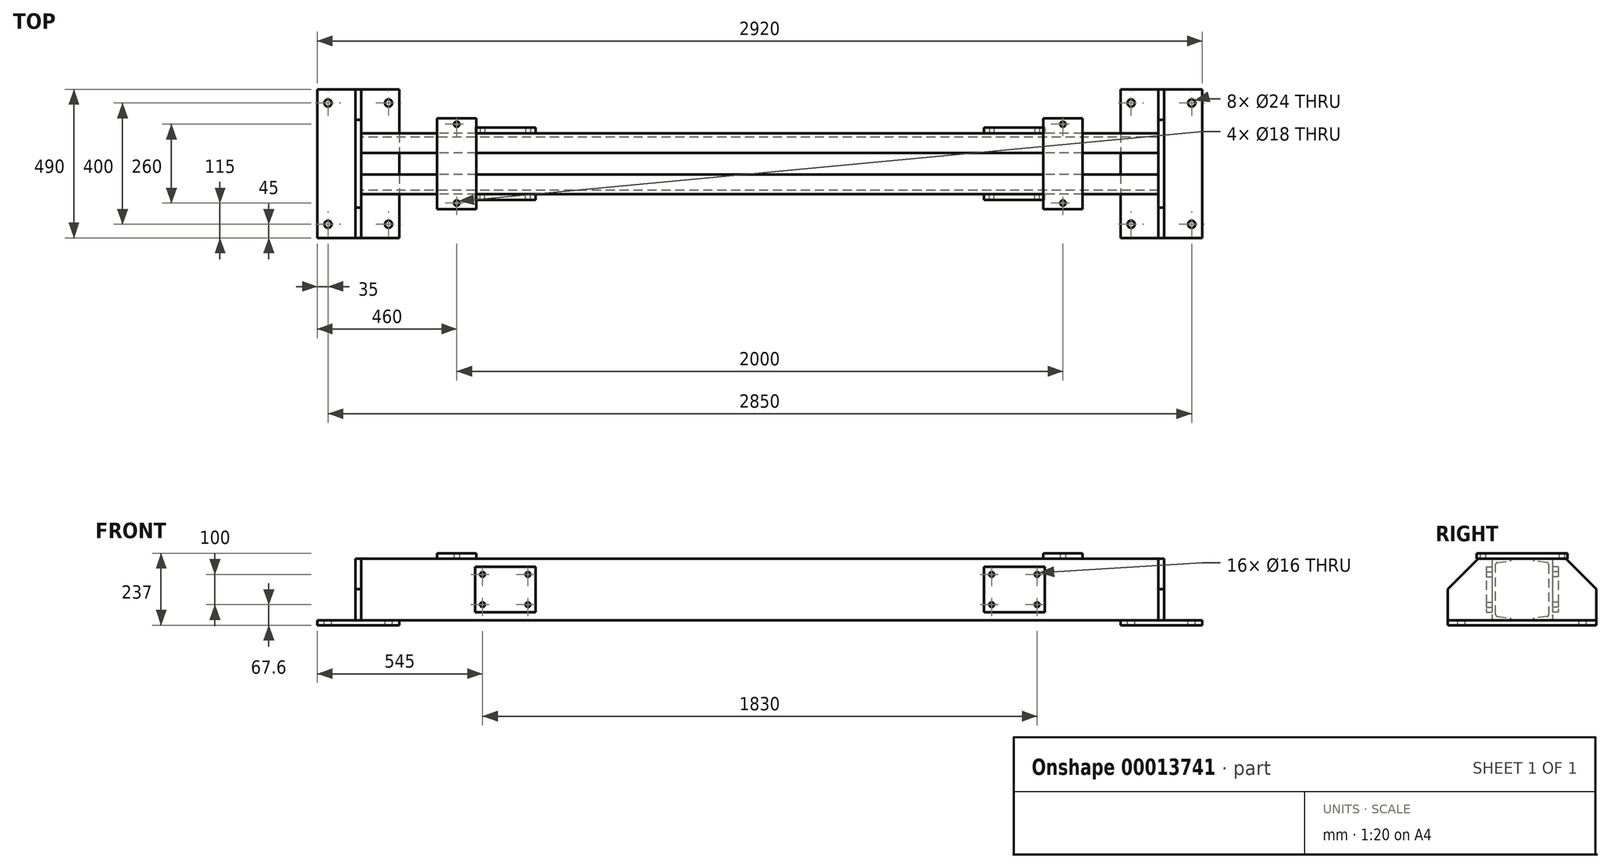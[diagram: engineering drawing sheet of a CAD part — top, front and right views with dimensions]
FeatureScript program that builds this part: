
annotation { "Feature Type Name" : "Feature", "Feature Type Description" : "" }
export const myFeature = defineFeature(function(context is Context, id is Id, definition is map)
    precondition{}
    {
        {
            var Q0;
            Q0=qCreatedBy(makeId("Right.planeOp"),FACE);
            var sketch = newSketch(context, id + "F0", { "sketchPlane" : qUnion([Q0])});
            skLineSegment(sketch, "E0", {"start": v(0, 81.85) * mm, "end": v(0, -95.58) * mm, "construction": true});
            skLineSegment(sketch, "E1", {"start": v(-119.35, 0) * mm, "end": v(122.16, 0) * mm, "construction": true});
            skLineSegment(sketch, "E2.0", {"start": v(-100, 101.6) * mm, "end": v(-100, 0) * mm});
            skLineSegment(sketch, "E3.0", {"start": v(-100, 101.6) * mm, "end": v(-35.8, 101.6) * mm});
            skLineSegment(sketch, "E4.0", {"start": v(-87.6, 82.16) * mm, "end": v(-87.6, 0) * mm});
            skLineSegment(sketch, "E5.0", {"start": v(-35.8, 88.1) * mm, "end": v(122.16, 88.1) * mm, "construction": true});
            skLineSegment(sketch, "E6.0", {"start": v(-35.8, 101.6) * mm, "end": v(-35.8, 99.47) * mm});
            skLineSegment(sketch, "E7", {"start": v(-81.71, 88.9) * mm, "end": v(-40.13, 94.51) * mm});
            skPoint(sketch, "E8.visualSharp", {"position": v(-35.8, 95.1) * mm});
            skArc(sketch, "E8.filletArc", {"start": v(-40.13, 94.51) * mm, "mid": v(-37.04, 96.18) * mm, "end": v(-35.8, 99.47) * mm});
            skPoint(sketch, "E9.visualSharp", {"position": v(-87.6, 88.1) * mm});
            skArc(sketch, "E9.filletArc", {"start": v(-81.71, 88.9) * mm, "mid": v(-85.92, 86.63) * mm, "end": v(-87.6, 82.16) * mm});
            skArc(sketch, "E10.0.MirrorCS", {"start": v(-40.13, -94.51) * mm, "mid": v(-37.04, -96.18) * mm, "end": v(-35.8, -99.47) * mm});
            skLineSegment(sketch, "E10.1.MirrorCS", {"start": v(-35.8, -101.6) * mm, "end": v(-35.8, -99.47) * mm});
            skArc(sketch, "E10.2.MirrorCS", {"start": v(-81.71, -88.9) * mm, "mid": v(-85.92, -86.63) * mm, "end": v(-87.6, -82.16) * mm});
            skPoint(sketch, "E10.3.MirrorP", {"position": v(-87.6, -88.1) * mm});
            skLineSegment(sketch, "E10.4.MirrorCS", {"start": v(-100, -101.6) * mm, "end": v(-100, 0) * mm});
            skLineSegment(sketch, "E10.5.MirrorCS", {"start": v(-87.6, -82.16) * mm, "end": v(-87.6, 0) * mm});
            skLineSegment(sketch, "E10.6.MirrorCS", {"start": v(-81.71, -88.9) * mm, "end": v(-40.13, -94.51) * mm});
            skLineSegment(sketch, "E10.7.MirrorCS", {"start": v(-100, -101.6) * mm, "end": v(-35.8, -101.6) * mm});
            skPoint(sketch, "E10.8.MirrorP", {"position": v(-35.8, -95.1) * mm});
            skLineSegment(sketch, "E11.0.MirrorCS", {"start": v(35.8, -101.6) * mm, "end": v(35.8, -99.47) * mm});
            skArc(sketch, "E11.1.MirrorCS", {"start": v(40.13, 94.51) * mm, "mid": v(37.04, 96.18) * mm, "end": v(35.8, 99.47) * mm});
            skLineSegment(sketch, "E11.2.MirrorCS", {"start": v(35.8, 101.6) * mm, "end": v(35.8, 99.47) * mm});
            skArc(sketch, "E11.3.MirrorCS", {"start": v(40.13, -94.51) * mm, "mid": v(37.04, -96.18) * mm, "end": v(35.8, -99.47) * mm});
            skArc(sketch, "E11.4.MirrorCS", {"start": v(81.71, 88.9) * mm, "mid": v(85.92, 86.63) * mm, "end": v(87.6, 82.16) * mm});
            skArc(sketch, "E11.5.MirrorCS", {"start": v(81.71, -88.9) * mm, "mid": v(85.92, -86.63) * mm, "end": v(87.6, -82.16) * mm});
            skLineSegment(sketch, "E11.6.MirrorCS", {"start": v(100, -101.6) * mm, "end": v(35.8, -101.6) * mm});
            skLineSegment(sketch, "E11.7.MirrorCS", {"start": v(100, -101.6) * mm, "end": v(100, 0) * mm});
            skLineSegment(sketch, "E11.8.MirrorCS", {"start": v(81.71, -88.9) * mm, "end": v(40.13, -94.51) * mm});
            skLineSegment(sketch, "E11.9.MirrorCS", {"start": v(87.6, -82.16) * mm, "end": v(87.6, 0) * mm});
            skPoint(sketch, "E11.10.MirrorP", {"position": v(87.6, -88.1) * mm});
            skPoint(sketch, "E11.11.MirrorP", {"position": v(35.8, 95.1) * mm});
            skPoint(sketch, "E11.12.MirrorP", {"position": v(35.8, -95.1) * mm});
            skLineSegment(sketch, "E11.13.MirrorCS", {"start": v(81.71, 88.9) * mm, "end": v(40.13, 94.51) * mm});
            skLineSegment(sketch, "E11.14.MirrorCS", {"start": v(100, 101.6) * mm, "end": v(35.8, 101.6) * mm});
            skPoint(sketch, "E11.15.MirrorP", {"position": v(87.6, 88.1) * mm});
            skLineSegment(sketch, "E11.16.MirrorCS", {"start": v(100, 101.6) * mm, "end": v(100, 0) * mm});
            skLineSegment(sketch, "E11.17.MirrorCS", {"start": v(87.6, 82.16) * mm, "end": v(87.6, 0) * mm});
            skSolve(sketch);
        }
        {
            var Q0;
            Q0=qSketchRegion(id+"F0",true);
            extrude(context, id + "F1", {"entities" : qUnion([Q0]), "endBound" : BoundingType.SYMMETRIC, "depth" : 2631 * mm});
        }
        {
            var Q0;
            Q0=makeQuery(id+"F1.opExtrude","CAP_FACE",FACE,{"disambiguationData":[OSD([sQuery(id+"F0.wireOp",EDGE,"E2.0"),sQuery(id+"F0.wireOp",EDGE,"E3.0"),sQuery(id+"F0.wireOp",EDGE,"E4.0"),sQuery(id+"F0.wireOp",EDGE,"E6.0"),sQuery(id+"F0.wireOp",EDGE,"E7"),sQuery(id+"F0.wireOp",EDGE,"E8.filletArc"),sQuery(id+"F0.wireOp",EDGE,"E9.filletArc"),sQuery(id+"F0.wireOp",EDGE,"E10.0.MirrorCS"),sQuery(id+"F0.wireOp",EDGE,"E10.1.MirrorCS"),sQuery(id+"F0.wireOp",EDGE,"E10.2.MirrorCS"),sQuery(id+"F0.wireOp",EDGE,"E10.4.MirrorCS"),sQuery(id+"F0.wireOp",EDGE,"E10.5.MirrorCS"),sQuery(id+"F0.wireOp",EDGE,"E10.6.MirrorCS"),sQuery(id+"F0.wireOp",EDGE,"E10.7.MirrorCS")])],"isStart":false});
            var sketch = newSketch(context, id + "F2", { "sketchPlane" : qUnion([Q0])});
            skLineSegment(sketch, "E12", {"start": v(0, 0) * mm, "end": v(0, -156.9) * mm, "construction": true});
            skLineSegment(sketch, "E13.0", {"start": v(-245, 1.6) * mm, "end": v(-245, -101.6) * mm});
            skLineSegment(sketch, "E14.0", {"start": v(-245, -101.6) * mm, "end": v(0, -101.6) * mm});
            skLineSegment(sketch, "E15.0", {"start": v(-145, 101.6) * mm, "end": v(0, 101.6) * mm});
            skPoint(sketch, "E16.orphan", {"position": v(-100, -101.6) * mm});
            skPoint(sketch, "E17.orphan", {"position": v(-100, 101.6) * mm});
            skPoint(sketch, "E18.orphan", {"position": v(-35.8, 101.6) * mm});
            skPoint(sketch, "E19.orphan", {"position": v(-35.8, -101.6) * mm});
            skLineSegment(sketch, "E20.0", {"start": v(-145, 101.6) * mm, "end": v(-145, -101.6) * mm, "construction": true});
            skLineSegment(sketch, "E21.0", {"start": v(-245, 1.6) * mm, "end": v(0, 1.6) * mm, "construction": true});
            skLineSegment(sketch, "E22", {"start": v(-245, 1.6) * mm, "end": v(-145, 101.6) * mm});
            skLineSegment(sketch, "E23.0.MirrorCS", {"start": v(245, 1.6) * mm, "end": v(245, -101.6) * mm});
            skLineSegment(sketch, "E23.1.MirrorCS", {"start": v(245, -101.6) * mm, "end": v(0, -101.6) * mm});
            skLineSegment(sketch, "E24.0.MirrorCS", {"start": v(245, 1.6) * mm, "end": v(145, 101.6) * mm});
            skLineSegment(sketch, "E25.0.MirrorCS", {"start": v(145, 101.6) * mm, "end": v(0, 101.6) * mm});
            skSolve(sketch);
        }
        {
            var Q0;
            Q0=qSketchRegion(id+"F2",true);
            extrude(context, id + "F3", {"entities" : qUnion([Q0]), "depth" : 19 * mm});
        }
        {
            var Q0;
            Q0=makeQuery(id+"F3.opExtrude","SWEPT_BODY",BODY,{"disambiguationData":[OSD([sQuery(id+"F2.wireOp",EDGE,"E13.0"),sQuery(id+"F2.wireOp",EDGE,"E14.0"),sQuery(id+"F2.wireOp",EDGE,"E15.0"),sQuery(id+"F2.wireOp",EDGE,"E22"),sQuery(id+"F2.wireOp",EDGE,"E23.0.MirrorCS"),sQuery(id+"F2.wireOp",EDGE,"E23.1.MirrorCS"),sQuery(id+"F2.wireOp",EDGE,"E24.0.MirrorCS"),sQuery(id+"F2.wireOp",EDGE,"E25.0.MirrorCS")])]});
            var Q1;
            Q1=qCreatedBy(makeId("Right.planeOp"),FACE);
            mirror(context, id + "F4", {"entities" : qUnion([Q0]), "mirrorPlane" : qUnion([Q1])});
        }
        {
            var Q0;
            Q0=makeQuery(id+"F1.opExtrude","SWEPT_FACE",FACE,{"disambiguationData":[OSD([sQuery(id+"F0.wireOp",EDGE,"E10.7.MirrorCS")])]});
            var sketch = newSketch(context, id + "F5", { "sketchPlane" : qUnion([Q0])});
            skLineSegment(sketch, "E26", {"start": v(0, 0) * mm, "end": v(0, 513.83) * mm, "construction": true});
            skLineSegment(sketch, "E27", {"start": v(0, 0) * mm, "end": v(1410.8, 0) * mm, "construction": true});
            skLineSegment(sketch, "E28.0", {"start": v(1325, 0) * mm, "end": v(1325, 513.83) * mm, "construction": true});
            skLineSegment(sketch, "E29.0", {"start": v(1460, -245) * mm, "end": v(1460, 245) * mm});
            skLineSegment(sketch, "E30.0", {"start": v(1190, 245) * mm, "end": v(1460, 245) * mm});
            skLineSegment(sketch, "E31.0.MirrorCS", {"start": v(1190, -245) * mm, "end": v(1190, 245) * mm});
            skPoint(sketch, "E32.orphan", {"position": v(1190, 513.83) * mm});
            skPoint(sketch, "E33.orphan", {"position": v(1460, 513.83) * mm});
            skLineSegment(sketch, "E34.0.MirrorCS", {"start": v(1190, -245) * mm, "end": v(1460, -245) * mm});
            skPoint(sketch, "E35.orphan", {"position": v(1460, 0) * mm});
            skPoint(sketch, "E36.orphan", {"position": v(1190, 0) * mm});
            skLineSegment(sketch, "E37.0", {"start": v(0, 200) * mm, "end": v(1425, 200) * mm, "construction": true});
            skLineSegment(sketch, "E38.0", {"start": v(1425, 0) * mm, "end": v(1425, 200) * mm, "construction": true});
            skCircle(sketch, "E39", {"center": v(1425, 200) * mm, "radius": 12 * mm});
            skCircle(sketch, "E40.0.MirrorC", {"center": v(1425, -200) * mm, "radius": 12 * mm});
            skCircle(sketch, "E41.0.MirrorC", {"center": v(1225, -200) * mm, "radius": 12 * mm});
            skCircle(sketch, "E42.0.MirrorC", {"center": v(1225, 200) * mm, "radius": 12 * mm});
            skSolve(sketch);
        }
        {
            var Q0;
            Q0=qSketchRegion(id+"F5",true);
            extrude(context, id + "F6", {"entities" : qUnion([Q0]), "depth" : 16 * mm});
        }
        {
            var Q0;
            Q0=makeQuery(id+"F6.opExtrude","SWEPT_BODY",BODY,{"disambiguationData":[OSD([sQuery(id+"F5.wireOp",EDGE,"E29.0"),sQuery(id+"F5.wireOp",EDGE,"E30.0"),sQuery(id+"F5.wireOp",EDGE,"E31.0.MirrorCS"),sQuery(id+"F5.wireOp",EDGE,"E34.0.MirrorCS"),sQuery(id+"F5.wireOp",EDGE,"E39"),sQuery(id+"F5.wireOp",EDGE,"E40.0.MirrorC"),sQuery(id+"F5.wireOp",EDGE,"E41.0.MirrorC"),sQuery(id+"F5.wireOp",EDGE,"E42.0.MirrorC")])]});
            var Q1;
            Q1=qCreatedBy(makeId("Right.planeOp"),FACE);
            mirror(context, id + "F7", {"entities" : qUnion([Q0]), "mirrorPlane" : qUnion([Q1])});
        }
        {
            var Q0;
            Q0=makeQuery(id+"F1.opExtrude","SWEPT_FACE",FACE,{"disambiguationData":[OSD([sQuery(id+"F0.wireOp",EDGE,"E11.14.MirrorCS")])]});
            var sketch = newSketch(context, id + "F8", { "sketchPlane" : qUnion([Q0])});
            skLineSegment(sketch, "E43", {"start": v(0, 0) * mm, "end": v(0, 449.39) * mm, "construction": true});
            skLineSegment(sketch, "E44", {"start": v(0, 0) * mm, "end": v(1523.6, 0) * mm, "construction": true});
            skLineSegment(sketch, "E45.0", {"start": v(1000, 0) * mm, "end": v(1000, 449.39) * mm, "construction": true});
            skLineSegment(sketch, "E46.0", {"start": v(1000, 150) * mm, "end": v(1065, 150) * mm});
            skLineSegment(sketch, "E47.0", {"start": v(1065, 0) * mm, "end": v(1065, 150) * mm});
            skLineSegment(sketch, "E48.0.MirrorCS", {"start": v(1065, 0) * mm, "end": v(1065, -150) * mm});
            skLineSegment(sketch, "E49.0.MirrorCS", {"start": v(1000, -150) * mm, "end": v(1065, -150) * mm});
            skLineSegment(sketch, "E50.0.MirrorCS", {"start": v(1000, 150) * mm, "end": v(935, 150) * mm});
            skLineSegment(sketch, "E51.0.MirrorCS", {"start": v(935, 0) * mm, "end": v(935, 150) * mm});
            skLineSegment(sketch, "E52.0.MirrorCS", {"start": v(935, 0) * mm, "end": v(935, -150) * mm});
            skLineSegment(sketch, "E53.0.MirrorCS", {"start": v(1000, -150) * mm, "end": v(935, -150) * mm});
            skLineSegment(sketch, "E54.0", {"start": v(0, 130) * mm, "end": v(1523.6, 130) * mm, "construction": true});
            skCircle(sketch, "E55", {"center": v(1000, 130) * mm, "radius": 9 * mm});
            skCircle(sketch, "E56.0.MirrorC", {"center": v(1000, -130) * mm, "radius": 9 * mm});
            skSolve(sketch);
        }
        {
            var Q0;
            Q0=qSketchRegion(id+"F8",true);
            extrude(context, id + "F9", {"entities" : qUnion([Q0]), "depth" : 17.8 * mm});
        }
        {
            var Q0;
            Q0=makeQuery(id+"F9.opExtrude","SWEPT_BODY",BODY,{"disambiguationData":[OSD([sQuery(id+"F8.wireOp",EDGE,"E46.0"),sQuery(id+"F8.wireOp",EDGE,"E47.0"),sQuery(id+"F8.wireOp",EDGE,"E48.0.MirrorCS"),sQuery(id+"F8.wireOp",EDGE,"E49.0.MirrorCS"),sQuery(id+"F8.wireOp",EDGE,"E50.0.MirrorCS"),sQuery(id+"F8.wireOp",EDGE,"E51.0.MirrorCS"),sQuery(id+"F8.wireOp",EDGE,"E52.0.MirrorCS"),sQuery(id+"F8.wireOp",EDGE,"E53.0.MirrorCS"),sQuery(id+"F8.wireOp",EDGE,"E55"),sQuery(id+"F8.wireOp",EDGE,"E56.0.MirrorC")])]});
            var Q1;
            Q1=qCreatedBy(makeId("Right.planeOp"),FACE);
            mirror(context, id + "F10", {"entities" : qUnion([Q0]), "mirrorPlane" : qUnion([Q1])});
        }
        {
            var Q0;
            Q0=makeQuery(id+"F1.opExtrude","SWEPT_FACE",FACE,{"disambiguationData":[OSD([sQuery(id+"F0.wireOp",EDGE,"E11.7.MirrorCS"),sQuery(id+"F0.wireOp",EDGE,"E11.16.MirrorCS")])]});
            var sketch = newSketch(context, id + "F11", { "sketchPlane" : qUnion([Q0])});
            skLineSegment(sketch, "E57", {"start": v(0, 268.1) * mm, "end": v(0, -305.9) * mm, "construction": true});
            skLineSegment(sketch, "E58", {"start": v(0, 0) * mm, "end": v(-1422.02, 0) * mm, "construction": true});
            skLineSegment(sketch, "E59.0", {"start": v(-840, 268.1) * mm, "end": v(-840, -305.9) * mm, "construction": true});
            skLineSegment(sketch, "E60.0", {"start": v(-840, 75) * mm, "end": v(-940, 75) * mm});
            skLineSegment(sketch, "E61.0", {"start": v(-940, 75) * mm, "end": v(-940, 0) * mm});
            skLineSegment(sketch, "E62.0.MirrorCS", {"start": v(-840, 75) * mm, "end": v(-740, 75) * mm});
            skLineSegment(sketch, "E63.0.MirrorCS", {"start": v(-740, 75) * mm, "end": v(-740, 0) * mm});
            skLineSegment(sketch, "E64.0.MirrorCS", {"start": v(-940, -75) * mm, "end": v(-940, 0) * mm});
            skLineSegment(sketch, "E65.0.MirrorCS", {"start": v(-840, -75) * mm, "end": v(-940, -75) * mm});
            skLineSegment(sketch, "E66.0.MirrorCS", {"start": v(-840, -75) * mm, "end": v(-740, -75) * mm});
            skLineSegment(sketch, "E67.0.MirrorCS", {"start": v(-740, -75) * mm, "end": v(-740, 0) * mm});
            skLineSegment(sketch, "E68.0", {"start": v(-915, 268.1) * mm, "end": v(-915, -305.9) * mm, "construction": true});
            skLineSegment(sketch, "E69.0", {"start": v(0, 50) * mm, "end": v(-1422.02, 50) * mm, "construction": true});
            skCircle(sketch, "E70", {"center": v(-915, 50) * mm, "radius": 8 * mm});
            skCircle(sketch, "E71.0.MirrorC", {"center": v(-765, 50) * mm, "radius": 8 * mm});
            skCircle(sketch, "E72.0.MirrorC", {"center": v(-915, -50) * mm, "radius": 8 * mm});
            skCircle(sketch, "E73.0.MirrorC", {"center": v(-765, -50) * mm, "radius": 8 * mm});
            skCircle(sketch, "E74.0.MirrorC", {"center": v(915, 50) * mm, "radius": 8 * mm});
            skLineSegment(sketch, "E74.1.MirrorCS", {"start": v(840, 75) * mm, "end": v(940, 75) * mm});
            skCircle(sketch, "E74.2.MirrorC", {"center": v(765, 50) * mm, "radius": 8 * mm});
            skCircle(sketch, "E74.3.MirrorC", {"center": v(915, -50) * mm, "radius": 8 * mm});
            skCircle(sketch, "E74.4.MirrorC", {"center": v(765, -50) * mm, "radius": 8 * mm});
            skLineSegment(sketch, "E74.5.MirrorCS", {"start": v(740, -75) * mm, "end": v(740, 0) * mm});
            skLineSegment(sketch, "E74.6.MirrorCS", {"start": v(840, 268.1) * mm, "end": v(840, -305.9) * mm, "construction": true});
            skLineSegment(sketch, "E74.7.MirrorCS", {"start": v(840, -75) * mm, "end": v(740, -75) * mm});
            skLineSegment(sketch, "E74.8.MirrorCS", {"start": v(0, 0) * mm, "end": v(1422.02, 0) * mm, "construction": true});
            skLineSegment(sketch, "E74.9.MirrorCS", {"start": v(740, 75) * mm, "end": v(740, 0) * mm});
            skLineSegment(sketch, "E74.10.MirrorCS", {"start": v(940, 75) * mm, "end": v(940, 0) * mm});
            skLineSegment(sketch, "E74.11.MirrorCS", {"start": v(840, 75) * mm, "end": v(740, 75) * mm});
            skLineSegment(sketch, "E74.12.MirrorCS", {"start": v(940, -75) * mm, "end": v(940, 0) * mm});
            skLineSegment(sketch, "E74.13.MirrorCS", {"start": v(0, 50) * mm, "end": v(1422.02, 50) * mm, "construction": true});
            skLineSegment(sketch, "E74.14.MirrorCS", {"start": v(915, 268.1) * mm, "end": v(915, -305.9) * mm, "construction": true});
            skLineSegment(sketch, "E74.15.MirrorCS", {"start": v(840, -75) * mm, "end": v(940, -75) * mm});
            skSolve(sketch);
        }
        {
            var Q0;
            Q0=qSketchRegion(id+"F11",true);
            extrude(context, id + "F12", {"entities" : qUnion([Q0]), "depth" : 19 * mm});
        }
        {
            var Q0;
            Q0=makeQuery(id+"F12.opExtrude","SWEPT_BODY",BODY,{"disambiguationData":[OSD([sQuery(id+"F11.wireOp",EDGE,"E60.0"),sQuery(id+"F11.wireOp",EDGE,"E61.0"),sQuery(id+"F11.wireOp",EDGE,"E62.0.MirrorCS"),sQuery(id+"F11.wireOp",EDGE,"E63.0.MirrorCS"),sQuery(id+"F11.wireOp",EDGE,"E64.0.MirrorCS"),sQuery(id+"F11.wireOp",EDGE,"E65.0.MirrorCS"),sQuery(id+"F11.wireOp",EDGE,"E66.0.MirrorCS"),sQuery(id+"F11.wireOp",EDGE,"E67.0.MirrorCS"),sQuery(id+"F11.wireOp",EDGE,"E70"),sQuery(id+"F11.wireOp",EDGE,"E71.0.MirrorC"),sQuery(id+"F11.wireOp",EDGE,"E72.0.MirrorC"),sQuery(id+"F11.wireOp",EDGE,"E73.0.MirrorC")])]});
            var Q1;
            Q1=makeQuery(id+"F12.opExtrude","SWEPT_BODY",BODY,{"disambiguationData":[OSD([sQuery(id+"F11.wireOp",EDGE,"E74.0.MirrorC"),sQuery(id+"F11.wireOp",EDGE,"E74.1.MirrorCS"),sQuery(id+"F11.wireOp",EDGE,"E74.2.MirrorC"),sQuery(id+"F11.wireOp",EDGE,"E74.3.MirrorC"),sQuery(id+"F11.wireOp",EDGE,"E74.4.MirrorC"),sQuery(id+"F11.wireOp",EDGE,"E74.5.MirrorCS"),sQuery(id+"F11.wireOp",EDGE,"E74.7.MirrorCS"),sQuery(id+"F11.wireOp",EDGE,"E74.9.MirrorCS"),sQuery(id+"F11.wireOp",EDGE,"E74.10.MirrorCS"),sQuery(id+"F11.wireOp",EDGE,"E74.11.MirrorCS"),sQuery(id+"F11.wireOp",EDGE,"E74.12.MirrorCS"),sQuery(id+"F11.wireOp",EDGE,"E74.15.MirrorCS")])]});
            var Q2;
            Q2=qCreatedBy(makeId("Front.planeOp"),FACE);
            mirror(context, id + "F13", {"entities" : qUnion([Q0, Q1]), "mirrorPlane" : qUnion([Q2])});
        }
    });
